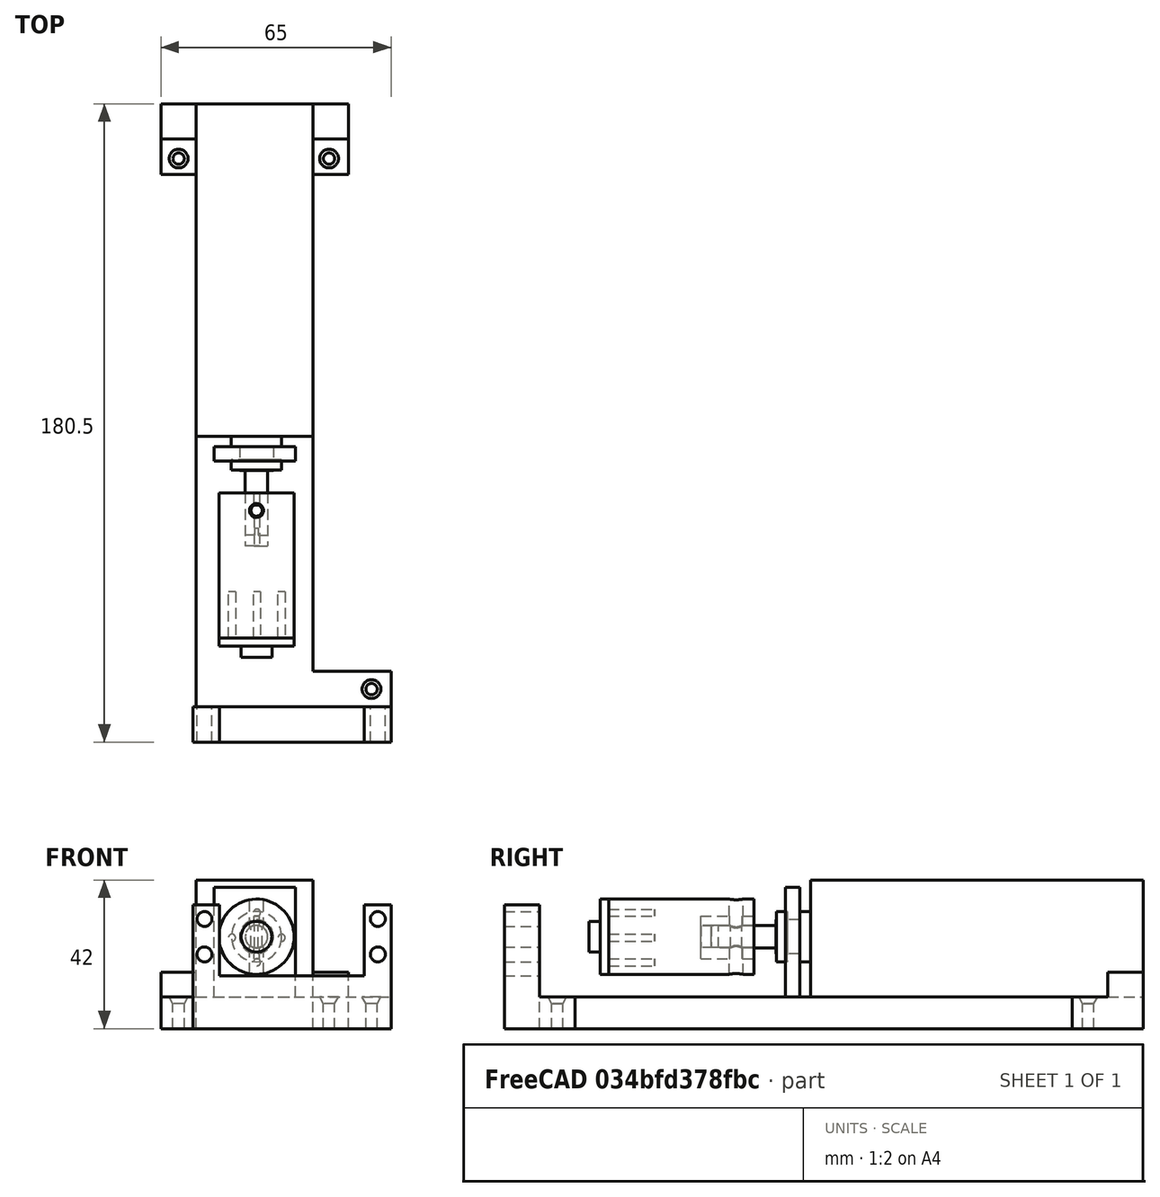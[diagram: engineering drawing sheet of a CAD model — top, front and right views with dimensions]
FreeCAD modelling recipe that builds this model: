
FCSTD DOCUMENT  (FreeCAD 0.19R24276 (Git))
Label: antennaTuner
License: All rights reserved
LicenseURL: http://en.wikipedia.org/wiki/All_rights_reserved
objects: Part::Cylinder×23, Part::Cut×18, Part::Box×14, Part::MultiFuse×12, Part::Cone×7, Mesh::Feature×1, Sketcher::SketchObject×1, PartDesign::Body×1, Part::Extrusion×1
note: 77 computed .brp shape members not serialized (recipe doc carries the construction recipe); baked Part::Feature solids carry a one-line shape summary decoded from their .brp

FEATURE [Mesh::Feature] MG996R_Servo_Model
  Placement = pos=(55,-27,10.5) rot=(0,1,0;4.71239rad)
FEATURE [Part::Box] Box  label="varicap001"
  AttacherType = Attacher::AttachEngine3D
  Height = 33
  Length = 33
  Placement = pos=(0,76,0) rot=(0,0,1;0rad)
  Width = 94
FEATURE [Part::Cylinder] Cylinder  label="shaft001"
  Angle = 360
  AttacherType = Attacher::AttachEngine3D
  Height = 3
  Placement = pos=(18,76,20) rot=(1,0,0;1.5708rad)
  Radius = 7.1
FEATURE [Part::Cylinder] Cylinder001  label="shaft002"
  Angle = 360
  AttacherType = Attacher::AttachEngine3D
  Height = 6.7
  Placement = pos=(18,73,20) rot=(1,0,0;1.5708rad)
  Radius = 4.8
FEATURE [Part::Cylinder] Cylinder002  label="shaft003"
  Angle = 360
  AttacherType = Attacher::AttachEngine3D
  Height = 19
  Placement = pos=(18,67,20) rot=(1,0,0;1.5708rad)
  Radius = 3.15
FEATURE [Part::Box] Box001  label="slit001"
  AttacherType = Attacher::AttachEngine3D
  Height = 6.4
  Length = 1
  Placement = pos=(17.5,48,16.8) rot=(0,0,1;0rad)
  Width = 2
FEATURE [Part::Cylinder] Cylinder003  label="hole001"
  Angle = 360
  AttacherType = Attacher::AttachEngine3D
  Height = 6.5
  Placement = pos=(18,55,16.7) rot=(0,0,1;0rad)
  Radius = 1.6
FEATURE [Part::Cylinder] Cylinder004  label="shaft004"
  Angle = 360
  AttacherType = Attacher::AttachEngine3D
  Height = 3
  Placement = pos=(18,69.4,20) rot=(1,0,0;1.5708rad)
  Radius = 7.1
FEATURE [Part::MultiFuse] Fusion
  Shapes = -> [Cylinder,Cylinder001,Cylinder002,Cylinder004]
FEATURE [Part::Cut] Cut
  Base = -> Fusion
  Tool = -> Cylinder003
FEATURE [Part::Cut] Cut001  label="wholeShaft001"
  Base = -> Cut
  Placement = pos=(-1,0,-3) rot=(0,0,1;0rad)
  Tool = -> Box001
FEATURE [Part::Cylinder] Cylinder005  label="bar001"
  Angle = 360
  AttacherType = Attacher::AttachEngine3D
  Height = 41
  Placement = pos=(18,60,20) rot=(1,0,0;1.5708rad)
  Radius = 10.63
FEATURE [Part::Cylinder] Cylinder006  label="barHole001"
  Angle = 360
  AttacherType = Attacher::AttachEngine3D
  Height = 15
  Placement = pos=(18,60,20) rot=(1,0,0;1.5708rad)
  Radius = 3.2
FEATURE [Part::Cylinder] Cylinder007  label="boltHole001"
  Angle = 360
  AttacherType = Attacher::AttachEngine3D
  Height = 22
  Placement = pos=(18,55,9) rot=(0,0,1;0rad)
  Radius = 2
FEATURE [Part::MultiFuse] Fusion001  label="cap001"
  Placement = pos=(1,0,3) rot=(0,0,1;0rad)
  Shapes = -> [Box,Cut001]
FEATURE [Part::Cylinder] Cylinder008  label="servoPlate001"
  Angle = 360
  AttacherType = Attacher::AttachEngine3D
  Height = 2.33
  Radius = 10.625
FEATURE [Part::Cylinder] Cylinder009  label="servoPlate002"
  Angle = 360
  AttacherType = Attacher::AttachEngine3D
  Height = 5.5
  Radius = 4.35
FEATURE [Part::Box] Box002  label="slit002"
  AttacherType = Attacher::AttachEngine3D
  Height = 12
  Length = 1.6
  Placement = pos=(17.3,45,13.8) rot=(0,0,1;0rad)
  Width = 15
FEATURE [Part::MultiFuse] Fusion002  label="servoPlate003"
  Placement = pos=(18,19,20) rot=(1,0,0;1.5708rad)
  Shapes = -> [Cylinder008,Cylinder009]
FEATURE [Part::MultiFuse] Fusion003  label="inner001"
  Shapes = -> [Cylinder006,Box002,Cylinder007]
FEATURE [Part::Cut] Cut002  label="bar002"
  Base = -> Cylinder005
  Tool = -> Fusion003
FEATURE [Sketcher::SketchObject] Sketch  label="servoHolesSketch001"
  FullyConstrained = false
  MapMode = 5
  Placement = pos=(0,0,0) rot=(1,0,0;1.5708rad)
  Support = -> [XZ_Plane]
  sketch-geometry (7):
    g0: Circle CenterX=11.094 CenterY=19.7113 CenterZ=0 NormalX=0 NormalY=0 NormalZ=1 AngleXU=0 Radius=1
    g1: Circle CenterX=25.094 CenterY=19.7113 CenterZ=0 NormalX=0 NormalY=0 NormalZ=1 AngleXU=0 Radius=1
    g2: Circle CenterX=18.1563 CenterY=26.7736 CenterZ=0 NormalX=0 NormalY=0 NormalZ=1 AngleXU=0 Radius=1
    g3: Circle CenterX=18.1563 CenterY=12.7736 CenterZ=0 NormalX=0 NormalY=0 NormalZ=1 AngleXU=0 Radius=1
    g4: LineSegment StartX=11.094 StartY=19.7113 StartZ=0 EndX=25.094 EndY=19.7113 EndZ=0
    g5: LineSegment StartX=18.1563 StartY=26.7736 StartZ=0 EndX=18.1563 EndY=12.7736 EndZ=0
    g6: LineSegment StartX=18.1563 StartY=26.7736 StartZ=0 EndX=11.094 EndY=19.7113 EndZ=0
  constraints (15):
    c: Radius(g1) = 1
    c: Radius(g0) = 1
    c: Radius(g2) = 1
    c: Radius(g3) = 1
    c: Coincident(g4,g0)
    c: Coincident(g4,g1)
    c: Horizontal(g4)
    c: Coincident(g5,g2)
    c: Coincident(g5,g3)
    c: Vertical(g5)
    c: DistanceY(g5,g5) = 14
    c: DistanceX(g4,g4) = 14
    c: Coincident(g6,g2)
    c: Coincident(g6,g0)
    c: Angle(g6,g5) = 0.785398
FEATURE [PartDesign::Body] Body
  Group = -> [Sketch]
  Origin = -> Origin
  Placement = pos=(0,19,0) rot=(0,0,1;0rad)
FEATURE [Part::Extrusion] Extrude  label="servoHoles001"
  Base = -> Sketch
  Dir = (0,-1,2e-16)
  DirMode = 2
  FaceMakerClass = Part::FaceMakerBullseye
  LengthFwd = 13
  LengthRev = 0
  Placement = pos=(0,32,0) rot=(0,0,1;0rad)
  Solid = true
  Symmetric = false
FEATURE [Part::Cut] Cut003  label="connect001"
  Base = -> Cut002
  Tool = -> Extrude
FEATURE [Part::Box] Box003  label="frame001"
  AttacherType = Attacher::AttachEngine3D
  Height = 9
  Length = 33
  Placement = pos=(1,-10.5,-6) rot=(0,0,1;0rad)
  Width = 180.5
FEATURE [Part::Box] Box005  label="frame003"
  AttacherType = Attacher::AttachEngine3D
  Height = 31
  Length = 23
  Placement = pos=(6,69,3) rot=(0,0,1;0rad)
  Width = 4
FEATURE [Part::Box] Box006  label="frame004"
  AttacherType = Attacher::AttachEngine3D
  Height = 26
  Length = 56
  Placement = pos=(0,-10.5,3) rot=(0,0,1;0rad)
  Width = 10
FEATURE [Part::Cylinder] Cylinder010  label="servoAttach001"
  Angle = 360
  AttacherType = Attacher::AttachEngine3D
  Height = 10
  Placement = pos=(3.3,-10.5,25) rot=(1,0,0;4.71239rad)
  Radius = 2.125
FEATURE [Part::Cylinder] Cylinder011  label="servoAttach002"
  Angle = 360
  AttacherType = Attacher::AttachEngine3D
  Height = 10
  Placement = pos=(3.3,-10.5,15) rot=(-1,0,0;1.5708rad)
  Radius = 2.125
FEATURE [Part::Cylinder] Cylinder012  label="servoAttach003"
  Angle = 360
  AttacherType = Attacher::AttachEngine3D
  Height = 10
  Placement = pos=(52.3,-10.5,25) rot=(-1,0,0;1.5708rad)
  Radius = 2.125
FEATURE [Part::Cylinder] Cylinder013  label="servoAttach004"
  Angle = 360
  AttacherType = Attacher::AttachEngine3D
  Height = 10
  Placement = pos=(52.3,-10.5,15) rot=(-1,0,0;1.5708rad)
  Radius = 2.125
FEATURE [Part::Box] Box007  label="frame005"
  AttacherType = Attacher::AttachEngine3D
  Height = 20
  Length = 41
  Placement = pos=(7.5,-10.5,9) rot=(0,0,1;0rad)
  Width = 10
FEATURE [Part::Box] Box008  label="frame006"
  AttacherType = Attacher::AttachEngine3D
  Height = 9
  Length = 22
  Placement = pos=(34,-10.5,-6) rot=(0,0,1;0rad)
  Width = 10
FEATURE [Part::Box] Box009  label="frame007"
  AttacherType = Attacher::AttachEngine3D
  Height = 9
  Length = 1
  Placement = pos=(0,-10.5,-6) rot=(0,0,1;0rad)
  Width = 10
FEATURE [Part::Cone] Cone009  label="wheelScrew006"
  Angle = 360
  AttacherType = Attacher::AttachEngine3D
  Height = 2
  Placement = pos=(9,-124,-12) rot=(0,0,1;0rad)
  Radius1 = 1.6
  Radius2 = 2.65
FEATURE [Part::Cylinder] Cylinder140  label="wheelScrew005"
  Angle = 360
  AttacherType = Attacher::AttachEngine3D
  Height = 7
  Placement = pos=(9,-124,-19) rot=(0,0,1;0rad)
  Radius = 1.6
FEATURE [Part::MultiFuse] Fusion007043  label="fullScrew001"
  Placement = pos=(29.5,278.5,13) rot=(0,0,1;0rad)
  Shapes = -> [Cone009,Cylinder140]
FEATURE [Part::Cone] Cone010  label="wheelScrew007"
  Angle = 360
  AttacherType = Attacher::AttachEngine3D
  Height = 2
  Placement = pos=(9,-124,-12) rot=(0,0,1;0rad)
  Radius1 = 1.6
  Radius2 = 2.65
FEATURE [Part::Cylinder] Cylinder141  label="wheelScrew008"
  Angle = 360
  AttacherType = Attacher::AttachEngine3D
  Height = 7
  Placement = pos=(9,-124,-19) rot=(0,0,1;0rad)
  Radius = 1.6
FEATURE [Part::MultiFuse] Fusion007045  label="fullScrew002"
  Placement = pos=(17,318,13) rot=(0,0,1;0rad)
  Shapes = -> [Cone010,Cylinder141]
FEATURE [Part::Cone] Cone011  label="wheelScrew009"
  Angle = 360
  AttacherType = Attacher::AttachEngine3D
  Height = 2
  Placement = pos=(9,-124,-12) rot=(0,0,1;0rad)
  Radius1 = 1.6
  Radius2 = 2.65
FEATURE [Part::Cylinder] Cylinder142  label="wheelScrew010"
  Angle = 360
  AttacherType = Attacher::AttachEngine3D
  Height = 7
  Placement = pos=(9,-124,-19) rot=(0,0,1;0rad)
  Radius = 1.6
FEATURE [Part::MultiFuse] Fusion007046  label="fullScrew003"
  Placement = pos=(-1,318,13) rot=(0,0,1;0rad)
  Shapes = -> [Cone011,Cylinder142]
FEATURE [Part::Cone] Cone012  label="wheelScrew011"
  Angle = 360
  AttacherType = Attacher::AttachEngine3D
  Height = 2
  Placement = pos=(9,-124,-12) rot=(0,0,1;0rad)
  Radius1 = 1.6
  Radius2 = 2.65
FEATURE [Part::Cylinder] Cylinder143  label="wheelScrew012"
  Angle = 360
  AttacherType = Attacher::AttachEngine3D
  Height = 7
  Placement = pos=(9,-124,-19) rot=(0,0,1;0rad)
  Radius = 1.6
FEATURE [Part::MultiFuse] Fusion007047  label="fullScrew004"
  Placement = pos=(-1,88,13) rot=(0,0,1;0rad)
  Shapes = -> [Cone012,Cylinder143]
FEATURE [Part::Cone] Cone013  label="wheelScrew013"
  Angle = 360
  AttacherType = Attacher::AttachEngine3D
  Height = 2
  Placement = pos=(9,-124,-12) rot=(0,0,1;0rad)
  Radius1 = 1.6
  Radius2 = 2.65
FEATURE [Part::Cylinder] Cylinder144  label="wheelScrew014"
  Angle = 360
  AttacherType = Attacher::AttachEngine3D
  Height = 7
  Placement = pos=(9,-124,-19) rot=(0,0,1;0rad)
  Radius = 1.6
FEATURE [Part::MultiFuse] Fusion007048  label="fullScrew005"
  Placement = pos=(17,88,13) rot=(0,0,1;0rad)
  Shapes = -> [Cone013,Cylinder144]
FEATURE [Part::Cylinder] Cylinder145  label="insert001"
  Angle = 360
  AttacherType = Attacher::AttachEngine3D
  Height = 10
  Placement = pos=(17.5,180.5,-7) rot=(0,0,1;0rad)
  Radius = 3.45
FEATURE [Part::Cut] Cut005
  Base = -> Box006
  Tool = -> Box007
FEATURE [Part::Box] Box012  label="frame008"
  AttacherType = Attacher::AttachEngine3D
  Height = 16
  Length = 10
  Placement = pos=(34,160,-6) rot=(0,0,1;0rad)
  Width = 10
FEATURE [Part::Box] Box013  label="frame009"
  AttacherType = Attacher::AttachEngine3D
  Height = 16
  Length = 10
  Placement = pos=(-9,160,-6) rot=(0,0,1;0rad)
  Width = 10
FEATURE [Part::Box] Box014  label="frame010"
  AttacherType = Attacher::AttachEngine3D
  Height = 9
  Length = 22
  Placement = pos=(34,-0.5,-6) rot=(0,0,1;0rad)
  Width = 10
FEATURE [Part::Box] Box015  label="frame011"
  AttacherType = Attacher::AttachEngine3D
  Height = 9
  Length = 10
  Placement = pos=(34,150,-6) rot=(0,0,1;0rad)
  Width = 10
FEATURE [Part::Box] Box016  label="frame012"
  AttacherType = Attacher::AttachEngine3D
  Height = 9
  Length = 10
  Placement = pos=(-9,150,-6) rot=(0,0,1;0rad)
  Width = 10
FEATURE [Part::MultiFuse] Fusion007049  label="base001"
  Shapes = -> [Box003,Cut005,Box005,Box008,Box009,Box012,Box013,Box014,Box015,Box016]
FEATURE [Part::Cut] Cut006
  Base = -> Fusion007049
  Tool = -> Fusion007047
FEATURE [Part::Cut] Cut007
  Base = -> Cut006
  Tool = -> Fusion007048
FEATURE [Part::Cut] Cut008
  Base = -> Cut007
  Tool = -> Fusion007046
FEATURE [Part::Cut] Cut009
  Base = -> Cut008
  Tool = -> Fusion007045
FEATURE [Part::Cut] Cut010
  Base = -> Cut009
  Tool = -> Cylinder145
FEATURE [Part::Cut] Cut011
  Base = -> Cut010
  Tool = -> Cylinder011
FEATURE [Part::Cut] Cut012
  Base = -> Cut011
  Tool = -> Cylinder010
FEATURE [Part::Cut] Cut013
  Base = -> Cut012
  Tool = -> Cylinder013
FEATURE [Part::Cut] Cut014  label="base002"
  Base = -> Cut013
  Tool = -> Cylinder012
FEATURE [Part::Cone] Cone014  label="wheelScrew015"
  Angle = 360
  AttacherType = Attacher::AttachEngine3D
  Height = 2
  Placement = pos=(9,-124,-12) rot=(0,0,1;0rad)
  Radius1 = 1.6
  Radius2 = 2.65
FEATURE [Part::Cylinder] Cylinder146  label="wheelScrew016"
  Angle = 360
  AttacherType = Attacher::AttachEngine3D
  Height = 7
  Placement = pos=(9,-124,-19) rot=(0,0,1;0rad)
  Radius = 1.6
FEATURE [Part::MultiFuse] Fusion007050  label="fullScrew006"
  Placement = pos=(-13,278.5,13) rot=(0,0,1;0rad)
  Shapes = -> [Cone014,Cylinder146]
FEATURE [Part::Cone] Cone015  label="wheelScrew017"
  Angle = 360
  AttacherType = Attacher::AttachEngine3D
  Height = 2
  Placement = pos=(9,-124,-12) rot=(0,0,1;0rad)
  Radius1 = 1.6
  Radius2 = 2.65
FEATURE [Part::Cylinder] Cylinder147  label="wheelScrew018"
  Angle = 360
  AttacherType = Attacher::AttachEngine3D
  Height = 7
  Placement = pos=(9,-124,-19) rot=(0,0,1;0rad)
  Radius = 1.6
FEATURE [Part::MultiFuse] Fusion007051  label="fullScrew007"
  Placement = pos=(41.5,128.5,13) rot=(0,0,1;0rad)
  Shapes = -> [Cone015,Cylinder147]
FEATURE [Part::Cut] Cut015
  Base = -> Cut014
  Tool = -> Fusion007043
FEATURE [Part::Cut] Cut016
  Base = -> Cut015
  Tool = -> Fusion007050
FEATURE [Part::Cut] Cut017  label="base003"
  Base = -> Cut016
  Tool = -> Fusion007051
FEATURE [Part::Cylinder] Cylinder148  label="hole002"
  Angle = 360
  AttacherType = Attacher::AttachEngine3D
  Height = 6.7
  Placement = pos=(18,73,20) rot=(1,0,0;1.5708rad)
  Radius = 4.8
FEATURE [Part::Cut] Cut018  label="base004"
  Base = -> Cut017
  Tool = -> Cylinder148
